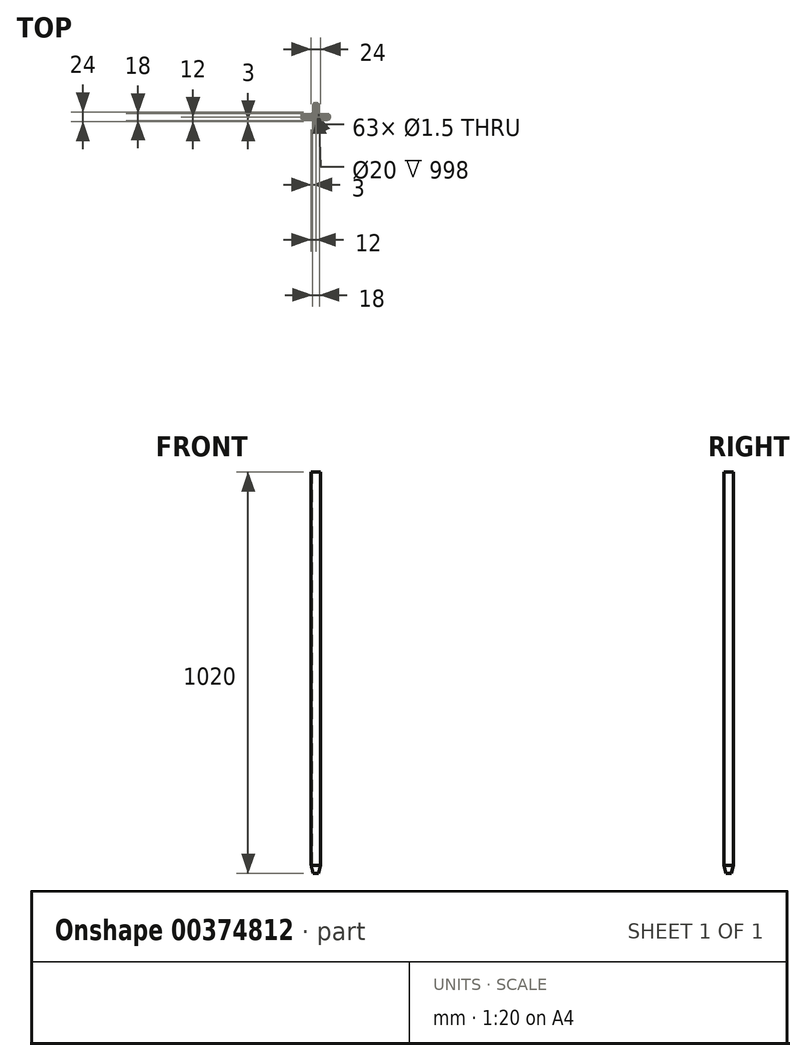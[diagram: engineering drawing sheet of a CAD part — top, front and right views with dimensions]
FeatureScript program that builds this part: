
annotation { "Feature Type Name" : "Feature", "Feature Type Description" : "" }
export const myFeature = defineFeature(function(context is Context, id is Id, definition is map)
    precondition{}
    {
        {
            var Q0;
            Q0=qCreatedBy(makeId("Front.planeOp"),FACE);
            var sketch = newSketch(context, id + "F0", { "sketchPlane" : qUnion([Q0])});
            skLineSegment(sketch, "E0", {"start": v(-10, 1020) * mm, "end": v(-10, 22) * mm});
            skLineSegment(sketch, "E1", {"start": v(-10, 22) * mm, "end": v(0, 22) * mm});
            skLineSegment(sketch, "E2", {"start": v(0, 22) * mm, "end": v(0, 20) * mm});
            skLineSegment(sketch, "E3", {"start": v(0, 20) * mm, "end": v(-10, 20) * mm});
            skLineSegment(sketch, "E4", {"start": v(-10, 20) * mm, "end": v(-5, 0) * mm});
            skLineSegment(sketch, "E5", {"start": v(-5, 0) * mm, "end": v(-7, 0) * mm});
            skLineSegment(sketch, "E6", {"start": v(-7, 0) * mm, "end": v(-12, 20) * mm});
            skLineSegment(sketch, "E7", {"start": v(-12, 20) * mm, "end": v(-12, 1020) * mm});
            skLineSegment(sketch, "E8", {"start": v(-12, 1020) * mm, "end": v(-10, 1020) * mm});
            skLineSegment(sketch, "E9", {"start": v(0, 0) * mm, "end": v(0, 1020) * mm, "construction": true});
            skSolve(sketch);
        }
        {
            var Q0;
            Q0 = qSketchRegion(id + "F0", true);
            var Q1;
            Q1=sQuery(id+"F0.wireOp",EDGE,"E9");
            revolve(context, id + "F1", {"entities" : qUnion([Q0]), "axis" : qUnion([Q1]), "revolveType" : RevolveType.FULL});
        }
        {
            var Q0;
            Q0=makeQuery(id+"F1.opRevolve","SWEPT_FACE",FACE,{"disambiguationData":[OSD([sQuery(id+"F0.wireOp",EDGE,"E1")])]});
            var sketch = newSketch(context, id + "F2", { "sketchPlane" : qUnion([Q0])});
            skCircle(sketch, "E10", {"center": v(0, 0) * mm, "radius": 0.75 * mm});
            skCircle(sketch, "E11", {"center": v(0, 2.25) * mm, "radius": 0.75 * mm});
            skCircle(sketch, "E12", {"center": v(0, 4.5) * mm, "radius": 0.75 * mm});
            skCircle(sketch, "E13", {"center": v(0, 6.75) * mm, "radius": 0.75 * mm});
            skCircle(sketch, "E14", {"center": v(0, 9) * mm, "radius": 0.75 * mm});
            skCircle(sketch, "E15.1.0", {"center": v(-1.95, 1.13) * mm, "radius": 0.75 * mm});
            skCircle(sketch, "E15.2.0", {"center": v(-1.95, -1.12) * mm, "radius": 0.75 * mm});
            skCircle(sketch, "E16.1.3.0", {"center": v(0, -2.25) * mm, "radius": 0.75 * mm});
            skCircle(sketch, "E17.1.0", {"center": v(-2.25, 3.9) * mm, "radius": 0.75 * mm});
            skCircle(sketch, "E17.2.0", {"center": v(-3.9, 2.25) * mm, "radius": 0.75 * mm});
            skCircle(sketch, "E18.1.3.0", {"center": v(-4.5, 0) * mm, "radius": 0.75 * mm});
            skCircle(sketch, "E18.1.4.0", {"center": v(-3.9, -2.25) * mm, "radius": 0.75 * mm});
            skCircle(sketch, "E18.1.5.0", {"center": v(-2.25, -3.9) * mm, "radius": 0.75 * mm});
            skCircle(sketch, "E18.1.6.0", {"center": v(0, -4.5) * mm, "radius": 0.75 * mm});
            skCircle(sketch, "E18.1.7.0", {"center": v(2.25, -3.9) * mm, "radius": 0.75 * mm});
            skCircle(sketch, "E19.1.0", {"center": v(-2.09, 6.42) * mm, "radius": 0.75 * mm});
            skCircle(sketch, "E19.2.0", {"center": v(-3.97, 5.46) * mm, "radius": 0.75 * mm});
            skCircle(sketch, "E20.1.3.0", {"center": v(-5.46, 3.97) * mm, "radius": 0.75 * mm});
            skCircle(sketch, "E20.1.4.0", {"center": v(-6.42, 2.09) * mm, "radius": 0.75 * mm});
            skCircle(sketch, "E20.1.5.0", {"center": v(-6.75, 0) * mm, "radius": 0.75 * mm});
            skCircle(sketch, "E20.1.6.0", {"center": v(-6.42, -2.09) * mm, "radius": 0.75 * mm});
            skCircle(sketch, "E20.1.7.0", {"center": v(-5.46, -3.97) * mm, "radius": 0.75 * mm});
            skCircle(sketch, "E20.1.8.0", {"center": v(-3.97, -5.46) * mm, "radius": 0.75 * mm});
            skCircle(sketch, "E20.1.9.0", {"center": v(-2.09, -6.42) * mm, "radius": 0.75 * mm});
            skCircle(sketch, "E20.1.10.0", {"center": v(0, -6.75) * mm, "radius": 0.75 * mm});
            skCircle(sketch, "E20.1.11.0", {"center": v(2.09, -6.42) * mm, "radius": 0.75 * mm});
            skCircle(sketch, "E20.1.12.0", {"center": v(3.97, -5.46) * mm, "radius": 0.75 * mm});
            skCircle(sketch, "E20.1.13.0", {"center": v(5.46, -3.97) * mm, "radius": 0.75 * mm});
            skCircle(sketch, "E20.1.14.0", {"center": v(6.42, -2.09) * mm, "radius": 0.75 * mm});
            skCircle(sketch, "E20.1.15.0", {"center": v(6.75, 0) * mm, "radius": 0.75 * mm});
            skCircle(sketch, "E21.1.0", {"center": v(-2.33, 8.7) * mm, "radius": 0.75 * mm});
            skCircle(sketch, "E21.2.0", {"center": v(-4.5, 7.8) * mm, "radius": 0.75 * mm});
            skCircle(sketch, "E22.1.3.0", {"center": v(-6.36, 6.36) * mm, "radius": 0.75 * mm});
            skCircle(sketch, "E22.1.4.0", {"center": v(-7.8, 4.5) * mm, "radius": 0.75 * mm});
            skCircle(sketch, "E22.1.5.0", {"center": v(-8.7, 2.33) * mm, "radius": 0.75 * mm});
            skCircle(sketch, "E22.1.6.0", {"center": v(-9, 0) * mm, "radius": 0.75 * mm});
            skCircle(sketch, "E22.1.7.0", {"center": v(-8.7, -2.33) * mm, "radius": 0.75 * mm});
            skCircle(sketch, "E22.1.8.0", {"center": v(-7.8, -4.5) * mm, "radius": 0.75 * mm});
            skCircle(sketch, "E22.1.9.0", {"center": v(-6.36, -6.36) * mm, "radius": 0.75 * mm});
            skCircle(sketch, "E22.1.10.0", {"center": v(-4.5, -7.8) * mm, "radius": 0.75 * mm});
            skCircle(sketch, "E22.1.11.0", {"center": v(-2.33, -8.7) * mm, "radius": 0.75 * mm});
            skCircle(sketch, "E22.1.12.0", {"center": v(0, -9) * mm, "radius": 0.75 * mm});
            skCircle(sketch, "E22.1.13.0", {"center": v(2.33, -8.7) * mm, "radius": 0.75 * mm});
            skCircle(sketch, "E22.1.14.0", {"center": v(4.5, -7.8) * mm, "radius": 0.75 * mm});
            skCircle(sketch, "E22.1.15.0", {"center": v(6.36, -6.36) * mm, "radius": 0.75 * mm});
            skCircle(sketch, "E22.1.16.0", {"center": v(7.8, -4.5) * mm, "radius": 0.75 * mm});
            skCircle(sketch, "E22.1.17.0", {"center": v(8.7, -2.33) * mm, "radius": 0.75 * mm});
            skCircle(sketch, "E22.1.18.0", {"center": v(9, 0) * mm, "radius": 0.75 * mm});
            skCircle(sketch, "E22.1.19.0", {"center": v(8.7, 2.33) * mm, "radius": 0.75 * mm});
            skCircle(sketch, "E22.1.20.0", {"center": v(7.8, 4.5) * mm, "radius": 0.75 * mm});
            skCircle(sketch, "E22.1.21.0", {"center": v(6.36, 6.36) * mm, "radius": 0.75 * mm});
            skCircle(sketch, "E22.1.22.0", {"center": v(4.5, 7.8) * mm, "radius": 0.75 * mm});
            skCircle(sketch, "E22.1.23.0", {"center": v(2.33, 8.7) * mm, "radius": 0.75 * mm});
            skCircle(sketch, "E23.1.16.0", {"center": v(6.42, 2.09) * mm, "radius": 0.75 * mm});
            skCircle(sketch, "E23.1.17.0", {"center": v(5.46, 3.97) * mm, "radius": 0.75 * mm});
            skCircle(sketch, "E23.1.18.0", {"center": v(3.97, 5.46) * mm, "radius": 0.75 * mm});
            skCircle(sketch, "E23.1.19.0", {"center": v(2.09, 6.42) * mm, "radius": 0.75 * mm});
            skCircle(sketch, "E24.1.8.0", {"center": v(3.9, -2.25) * mm, "radius": 0.75 * mm});
            skCircle(sketch, "E24.1.9.0", {"center": v(4.5, 0) * mm, "radius": 0.75 * mm});
            skCircle(sketch, "E24.1.10.0", {"center": v(3.9, 2.25) * mm, "radius": 0.75 * mm});
            skCircle(sketch, "E24.1.11.0", {"center": v(2.25, 3.9) * mm, "radius": 0.75 * mm});
            skCircle(sketch, "E25.1.4.0", {"center": v(1.95, -1.13) * mm, "radius": 0.75 * mm});
            skCircle(sketch, "E25.1.5.0", {"center": v(1.95, 1.13) * mm, "radius": 0.75 * mm});
            skSolve(sketch);
        }
        {
            var Q0;
            Q0=makeQuery(id+"F2.imprint","IMPRINT",FACE,{"disambiguationData":[TD([[makeQuery(id+"F2.imprint","IMPRINT",EDGE,{"derivedFrom":sQuery(id+"F2.wireOp",EDGE,"E19.2.0")}),1.0]])]});
            var Q1;
            Q1=makeQuery(id+"F2.imprint","IMPRINT",FACE,{"disambiguationData":[TD([[makeQuery(id+"F2.imprint","IMPRINT",EDGE,{"derivedFrom":sQuery(id+"F2.wireOp",EDGE,"E22.1.3.0")}),1.0]])]});
            var Q2;
            Q2=makeQuery(id+"F2.imprint","IMPRINT",FACE,{"disambiguationData":[TD([[makeQuery(id+"F2.imprint","IMPRINT",EDGE,{"derivedFrom":sQuery(id+"F2.wireOp",EDGE,"E21.2.0")}),1.0]])]});
            var Q3;
            Q3=makeQuery(id+"F2.imprint","IMPRINT",FACE,{"disambiguationData":[TD([[makeQuery(id+"F2.imprint","IMPRINT",EDGE,{"derivedFrom":sQuery(id+"F2.wireOp",EDGE,"E19.1.0")}),1.0]])]});
            var Q4;
            Q4=makeQuery(id+"F2.imprint","IMPRINT",FACE,{"disambiguationData":[TD([[makeQuery(id+"F2.imprint","IMPRINT",EDGE,{"derivedFrom":sQuery(id+"F2.wireOp",EDGE,"E21.1.0")}),1.0]])]});
            var Q5;
            Q5=makeQuery(id+"F2.imprint","IMPRINT",FACE,{"disambiguationData":[TD([[makeQuery(id+"F2.imprint","IMPRINT",EDGE,{"derivedFrom":sQuery(id+"F2.wireOp",EDGE,"E14")}),1.0]])]});
            var Q6;
            Q6=makeQuery(id+"F2.imprint","IMPRINT",FACE,{"disambiguationData":[TD([[makeQuery(id+"F2.imprint","IMPRINT",EDGE,{"derivedFrom":sQuery(id+"F2.wireOp",EDGE,"E13")}),1.0]])]});
            var Q7;
            Q7=makeQuery(id+"F2.imprint","IMPRINT",FACE,{"disambiguationData":[TD([[makeQuery(id+"F2.imprint","IMPRINT",EDGE,{"derivedFrom":sQuery(id+"F2.wireOp",EDGE,"E23.1.19.0")}),1.0]])]});
            var Q8;
            Q8=makeQuery(id+"F2.imprint","IMPRINT",FACE,{"disambiguationData":[TD([[makeQuery(id+"F2.imprint","IMPRINT",EDGE,{"derivedFrom":sQuery(id+"F2.wireOp",EDGE,"E22.1.23.0")}),1.0]])]});
            var Q9;
            Q9=makeQuery(id+"F2.imprint","IMPRINT",FACE,{"disambiguationData":[TD([[makeQuery(id+"F2.imprint","IMPRINT",EDGE,{"derivedFrom":sQuery(id+"F2.wireOp",EDGE,"E22.1.22.0")}),1.0]])]});
            var Q10;
            Q10=makeQuery(id+"F2.imprint","IMPRINT",FACE,{"disambiguationData":[TD([[makeQuery(id+"F2.imprint","IMPRINT",EDGE,{"derivedFrom":sQuery(id+"F2.wireOp",EDGE,"E22.1.21.0")}),1.0]])]});
            var Q11;
            Q11=makeQuery(id+"F2.imprint","IMPRINT",FACE,{"disambiguationData":[TD([[makeQuery(id+"F2.imprint","IMPRINT",EDGE,{"derivedFrom":sQuery(id+"F2.wireOp",EDGE,"E23.1.18.0")}),1.0]])]});
            var Q12;
            Q12=makeQuery(id+"F2.imprint","IMPRINT",FACE,{"disambiguationData":[TD([[makeQuery(id+"F2.imprint","IMPRINT",EDGE,{"derivedFrom":sQuery(id+"F2.wireOp",EDGE,"E23.1.17.0")}),1.0]])]});
            var Q13;
            Q13=makeQuery(id+"F2.imprint","IMPRINT",FACE,{"disambiguationData":[TD([[makeQuery(id+"F2.imprint","IMPRINT",EDGE,{"derivedFrom":sQuery(id+"F2.wireOp",EDGE,"E22.1.20.0")}),1.0]])]});
            var Q14;
            Q14=makeQuery(id+"F2.imprint","IMPRINT",FACE,{"disambiguationData":[TD([[makeQuery(id+"F2.imprint","IMPRINT",EDGE,{"derivedFrom":sQuery(id+"F2.wireOp",EDGE,"E22.1.19.0")}),1.0]])]});
            var Q15;
            Q15=makeQuery(id+"F2.imprint","IMPRINT",FACE,{"disambiguationData":[TD([[makeQuery(id+"F2.imprint","IMPRINT",EDGE,{"derivedFrom":sQuery(id+"F2.wireOp",EDGE,"E23.1.16.0")}),1.0]])]});
            var Q16;
            Q16=makeQuery(id+"F2.imprint","IMPRINT",FACE,{"disambiguationData":[TD([[makeQuery(id+"F2.imprint","IMPRINT",EDGE,{"derivedFrom":sQuery(id+"F2.wireOp",EDGE,"E24.1.10.0")}),1.0]])]});
            var Q17;
            Q17=makeQuery(id+"F2.imprint","IMPRINT",FACE,{"disambiguationData":[TD([[makeQuery(id+"F2.imprint","IMPRINT",EDGE,{"derivedFrom":sQuery(id+"F2.wireOp",EDGE,"E25.1.5.0")}),1.0]])]});
            var Q18;
            Q18=makeQuery(id+"F2.imprint","IMPRINT",FACE,{"disambiguationData":[TD([[makeQuery(id+"F2.imprint","IMPRINT",EDGE,{"derivedFrom":sQuery(id+"F2.wireOp",EDGE,"E24.1.11.0")}),1.0]])]});
            var Q19;
            Q19=makeQuery(id+"F2.imprint","IMPRINT",FACE,{"disambiguationData":[TD([[makeQuery(id+"F2.imprint","IMPRINT",EDGE,{"derivedFrom":sQuery(id+"F2.wireOp",EDGE,"E12")}),1.0]])]});
            var Q20;
            Q20=makeQuery(id+"F2.imprint","IMPRINT",FACE,{"disambiguationData":[TD([[makeQuery(id+"F2.imprint","IMPRINT",EDGE,{"derivedFrom":sQuery(id+"F2.wireOp",EDGE,"E11")}),1.0]])]});
            var Q21;
            Q21=makeQuery(id+"F2.imprint","IMPRINT",FACE,{"disambiguationData":[TD([[makeQuery(id+"F2.imprint","IMPRINT",EDGE,{"derivedFrom":sQuery(id+"F2.wireOp",EDGE,"E17.1.0")}),1.0]])]});
            var Q22;
            Q22=makeQuery(id+"F2.imprint","IMPRINT",FACE,{"disambiguationData":[TD([[makeQuery(id+"F2.imprint","IMPRINT",EDGE,{"derivedFrom":sQuery(id+"F2.wireOp",EDGE,"E15.1.0")}),1.0]])]});
            var Q23;
            Q23=makeQuery(id+"F2.imprint","IMPRINT",FACE,{"disambiguationData":[TD([[makeQuery(id+"F2.imprint","IMPRINT",EDGE,{"derivedFrom":sQuery(id+"F2.wireOp",EDGE,"E17.2.0")}),1.0]])]});
            var Q24;
            Q24=makeQuery(id+"F2.imprint","IMPRINT",FACE,{"disambiguationData":[TD([[makeQuery(id+"F2.imprint","IMPRINT",EDGE,{"derivedFrom":sQuery(id+"F2.wireOp",EDGE,"E20.1.3.0")}),1.0]])]});
            var Q25;
            Q25=makeQuery(id+"F2.imprint","IMPRINT",FACE,{"disambiguationData":[TD([[makeQuery(id+"F2.imprint","IMPRINT",EDGE,{"derivedFrom":sQuery(id+"F2.wireOp",EDGE,"E22.1.4.0")}),1.0]])]});
            var Q26;
            Q26=makeQuery(id+"F2.imprint","IMPRINT",FACE,{"disambiguationData":[TD([[makeQuery(id+"F2.imprint","IMPRINT",EDGE,{"derivedFrom":sQuery(id+"F2.wireOp",EDGE,"E22.1.5.0")}),1.0]])]});
            var Q27;
            Q27=makeQuery(id+"F2.imprint","IMPRINT",FACE,{"disambiguationData":[TD([[makeQuery(id+"F2.imprint","IMPRINT",EDGE,{"derivedFrom":sQuery(id+"F2.wireOp",EDGE,"E20.1.4.0")}),1.0]])]});
            var Q28;
            Q28=makeQuery(id+"F2.imprint","IMPRINT",FACE,{"disambiguationData":[TD([[makeQuery(id+"F2.imprint","IMPRINT",EDGE,{"derivedFrom":sQuery(id+"F2.wireOp",EDGE,"E18.1.3.0")}),1.0]])]});
            var Q29;
            Q29=makeQuery(id+"F2.imprint","IMPRINT",FACE,{"disambiguationData":[TD([[makeQuery(id+"F2.imprint","IMPRINT",EDGE,{"derivedFrom":sQuery(id+"F2.wireOp",EDGE,"E10")}),1.0]])]});
            var Q30;
            Q30=makeQuery(id+"F2.imprint","IMPRINT",FACE,{"disambiguationData":[TD([[makeQuery(id+"F2.imprint","IMPRINT",EDGE,{"derivedFrom":sQuery(id+"F2.wireOp",EDGE,"E24.1.9.0")}),1.0]])]});
            var Q31;
            Q31=makeQuery(id+"F2.imprint","IMPRINT",FACE,{"disambiguationData":[TD([[makeQuery(id+"F2.imprint","IMPRINT",EDGE,{"derivedFrom":sQuery(id+"F2.wireOp",EDGE,"E20.1.15.0")}),1.0]])]});
            var Q32;
            Q32=makeQuery(id+"F2.imprint","IMPRINT",FACE,{"disambiguationData":[TD([[makeQuery(id+"F2.imprint","IMPRINT",EDGE,{"derivedFrom":sQuery(id+"F2.wireOp",EDGE,"E22.1.18.0")}),1.0]])]});
            var Q33;
            Q33=makeQuery(id+"F2.imprint","IMPRINT",FACE,{"disambiguationData":[TD([[makeQuery(id+"F2.imprint","IMPRINT",EDGE,{"derivedFrom":sQuery(id+"F2.wireOp",EDGE,"E25.1.4.0")}),1.0]])]});
            var Q34;
            Q34=makeQuery(id+"F2.imprint","IMPRINT",FACE,{"disambiguationData":[TD([[makeQuery(id+"F2.imprint","IMPRINT",EDGE,{"derivedFrom":sQuery(id+"F2.wireOp",EDGE,"E24.1.8.0")}),1.0]])]});
            var Q35;
            Q35=makeQuery(id+"F2.imprint","IMPRINT",FACE,{"disambiguationData":[TD([[makeQuery(id+"F2.imprint","IMPRINT",EDGE,{"derivedFrom":sQuery(id+"F2.wireOp",EDGE,"E20.1.14.0")}),1.0]])]});
            var Q36;
            Q36=makeQuery(id+"F2.imprint","IMPRINT",FACE,{"disambiguationData":[TD([[makeQuery(id+"F2.imprint","IMPRINT",EDGE,{"derivedFrom":sQuery(id+"F2.wireOp",EDGE,"E22.1.17.0")}),1.0]])]});
            var Q37;
            Q37=makeQuery(id+"F2.imprint","IMPRINT",FACE,{"disambiguationData":[TD([[makeQuery(id+"F2.imprint","IMPRINT",EDGE,{"derivedFrom":sQuery(id+"F2.wireOp",EDGE,"E22.1.16.0")}),1.0]])]});
            var Q38;
            Q38=makeQuery(id+"F2.imprint","IMPRINT",FACE,{"disambiguationData":[TD([[makeQuery(id+"F2.imprint","IMPRINT",EDGE,{"derivedFrom":sQuery(id+"F2.wireOp",EDGE,"E22.1.15.0")}),1.0]])]});
            var Q39;
            Q39=makeQuery(id+"F2.imprint","IMPRINT",FACE,{"disambiguationData":[TD([[makeQuery(id+"F2.imprint","IMPRINT",EDGE,{"derivedFrom":sQuery(id+"F2.wireOp",EDGE,"E20.1.13.0")}),1.0]])]});
            var Q40;
            Q40=makeQuery(id+"F2.imprint","IMPRINT",FACE,{"disambiguationData":[TD([[makeQuery(id+"F2.imprint","IMPRINT",EDGE,{"derivedFrom":sQuery(id+"F2.wireOp",EDGE,"E20.1.12.0")}),1.0]])]});
            var Q41;
            Q41=makeQuery(id+"F2.imprint","IMPRINT",FACE,{"disambiguationData":[TD([[makeQuery(id+"F2.imprint","IMPRINT",EDGE,{"derivedFrom":sQuery(id+"F2.wireOp",EDGE,"E22.1.14.0")}),1.0]])]});
            var Q42;
            Q42=makeQuery(id+"F2.imprint","IMPRINT",FACE,{"disambiguationData":[TD([[makeQuery(id+"F2.imprint","IMPRINT",EDGE,{"derivedFrom":sQuery(id+"F2.wireOp",EDGE,"E22.1.13.0")}),1.0]])]});
            var Q43;
            Q43=makeQuery(id+"F2.imprint","IMPRINT",FACE,{"disambiguationData":[TD([[makeQuery(id+"F2.imprint","IMPRINT",EDGE,{"derivedFrom":sQuery(id+"F2.wireOp",EDGE,"E22.1.12.0")}),1.0]])]});
            var Q44;
            Q44=makeQuery(id+"F2.imprint","IMPRINT",FACE,{"disambiguationData":[TD([[makeQuery(id+"F2.imprint","IMPRINT",EDGE,{"derivedFrom":sQuery(id+"F2.wireOp",EDGE,"E20.1.11.0")}),1.0]])]});
            var Q45;
            Q45=makeQuery(id+"F2.imprint","IMPRINT",FACE,{"disambiguationData":[TD([[makeQuery(id+"F2.imprint","IMPRINT",EDGE,{"derivedFrom":sQuery(id+"F2.wireOp",EDGE,"E18.1.7.0")}),1.0]])]});
            var Q46;
            Q46=makeQuery(id+"F2.imprint","IMPRINT",FACE,{"disambiguationData":[TD([[makeQuery(id+"F2.imprint","IMPRINT",EDGE,{"derivedFrom":sQuery(id+"F2.wireOp",EDGE,"E20.1.10.0")}),1.0]])]});
            var Q47;
            Q47=makeQuery(id+"F2.imprint","IMPRINT",FACE,{"disambiguationData":[TD([[makeQuery(id+"F2.imprint","IMPRINT",EDGE,{"derivedFrom":sQuery(id+"F2.wireOp",EDGE,"E18.1.6.0")}),1.0]])]});
            var Q48;
            Q48=makeQuery(id+"F2.imprint","IMPRINT",FACE,{"disambiguationData":[TD([[makeQuery(id+"F2.imprint","IMPRINT",EDGE,{"derivedFrom":sQuery(id+"F2.wireOp",EDGE,"E16.1.3.0")}),1.0]])]});
            var Q49;
            Q49=makeQuery(id+"F2.imprint","IMPRINT",FACE,{"disambiguationData":[TD([[makeQuery(id+"F2.imprint","IMPRINT",EDGE,{"derivedFrom":sQuery(id+"F2.wireOp",EDGE,"E15.2.0")}),1.0]])]});
            var Q50;
            Q50=makeQuery(id+"F2.imprint","IMPRINT",FACE,{"disambiguationData":[TD([[makeQuery(id+"F2.imprint","IMPRINT",EDGE,{"derivedFrom":sQuery(id+"F2.wireOp",EDGE,"E18.1.5.0")}),1.0]])]});
            var Q51;
            Q51=makeQuery(id+"F2.imprint","IMPRINT",FACE,{"disambiguationData":[TD([[makeQuery(id+"F2.imprint","IMPRINT",EDGE,{"derivedFrom":sQuery(id+"F2.wireOp",EDGE,"E20.1.9.0")}),1.0]])]});
            var Q52;
            Q52=makeQuery(id+"F2.imprint","IMPRINT",FACE,{"disambiguationData":[TD([[makeQuery(id+"F2.imprint","IMPRINT",EDGE,{"derivedFrom":sQuery(id+"F2.wireOp",EDGE,"E22.1.11.0")}),1.0]])]});
            var Q53;
            Q53=makeQuery(id+"F2.imprint","IMPRINT",FACE,{"disambiguationData":[TD([[makeQuery(id+"F2.imprint","IMPRINT",EDGE,{"derivedFrom":sQuery(id+"F2.wireOp",EDGE,"E22.1.10.0")}),1.0]])]});
            var Q54;
            Q54=makeQuery(id+"F2.imprint","IMPRINT",FACE,{"disambiguationData":[TD([[makeQuery(id+"F2.imprint","IMPRINT",EDGE,{"derivedFrom":sQuery(id+"F2.wireOp",EDGE,"E20.1.8.0")}),1.0]])]});
            var Q55;
            Q55=makeQuery(id+"F2.imprint","IMPRINT",FACE,{"disambiguationData":[TD([[makeQuery(id+"F2.imprint","IMPRINT",EDGE,{"derivedFrom":sQuery(id+"F2.wireOp",EDGE,"E18.1.4.0")}),1.0]])]});
            var Q56;
            Q56=makeQuery(id+"F2.imprint","IMPRINT",FACE,{"disambiguationData":[TD([[makeQuery(id+"F2.imprint","IMPRINT",EDGE,{"derivedFrom":sQuery(id+"F2.wireOp",EDGE,"E20.1.7.0")}),1.0]])]});
            var Q57;
            Q57=makeQuery(id+"F2.imprint","IMPRINT",FACE,{"disambiguationData":[TD([[makeQuery(id+"F2.imprint","IMPRINT",EDGE,{"derivedFrom":sQuery(id+"F2.wireOp",EDGE,"E22.1.9.0")}),1.0]])]});
            var Q58;
            Q58=makeQuery(id+"F2.imprint","IMPRINT",FACE,{"disambiguationData":[TD([[makeQuery(id+"F2.imprint","IMPRINT",EDGE,{"derivedFrom":sQuery(id+"F2.wireOp",EDGE,"E22.1.8.0")}),1.0]])]});
            var Q59;
            Q59=makeQuery(id+"F2.imprint","IMPRINT",FACE,{"disambiguationData":[TD([[makeQuery(id+"F2.imprint","IMPRINT",EDGE,{"derivedFrom":sQuery(id+"F2.wireOp",EDGE,"E22.1.7.0")}),1.0]])]});
            var Q60;
            Q60=makeQuery(id+"F2.imprint","IMPRINT",FACE,{"disambiguationData":[TD([[makeQuery(id+"F2.imprint","IMPRINT",EDGE,{"derivedFrom":sQuery(id+"F2.wireOp",EDGE,"E20.1.6.0")}),1.0]])]});
            var Q61;
            Q61=makeQuery(id+"F2.imprint","IMPRINT",FACE,{"disambiguationData":[TD([[makeQuery(id+"F2.imprint","IMPRINT",EDGE,{"derivedFrom":sQuery(id+"F2.wireOp",EDGE,"E20.1.5.0")}),1.0]])]});
            var Q62;
            Q62=makeQuery(id+"F2.imprint","IMPRINT",FACE,{"disambiguationData":[TD([[makeQuery(id+"F2.imprint","IMPRINT",EDGE,{"derivedFrom":sQuery(id+"F2.wireOp",EDGE,"E22.1.6.0")}),1.0]])]});
            var Q63;
            Q63=makeQuery(id+"F1.opRevolve","SWEPT_FACE",FACE,{"disambiguationData":[OSD([sQuery(id+"F0.wireOp",EDGE,"E3")])]});
            extrude(context, id + "F3", {"entities" : qUnion([Q0, Q1, Q2, Q3, Q4, Q5, Q6, Q7, Q8, Q9, Q10, Q11, Q12, Q13, Q14, Q15, Q16, Q17, Q18, Q19, Q20, Q21, Q22, Q23, Q24, Q25, Q26, Q27, Q28, Q29, Q30, Q31, Q32, Q33, Q34, Q35, Q36, Q37, Q38, Q39, Q40, Q41, Q42, Q43, Q44, Q45, Q46, Q47, Q48, Q49, Q50, Q51, Q52, Q53, Q54, Q55, Q56, Q57, Q58, Q59, Q60, Q61, Q62]), "operationType" : NewBodyOperationType.REMOVE, "endBound" : BoundingType.UP_TO_SURFACE, "oppositeDirection" : true, "endBoundEntityFace" : qUnion([Q63]), "depth" : 25.4 * mm});
        }
    });
